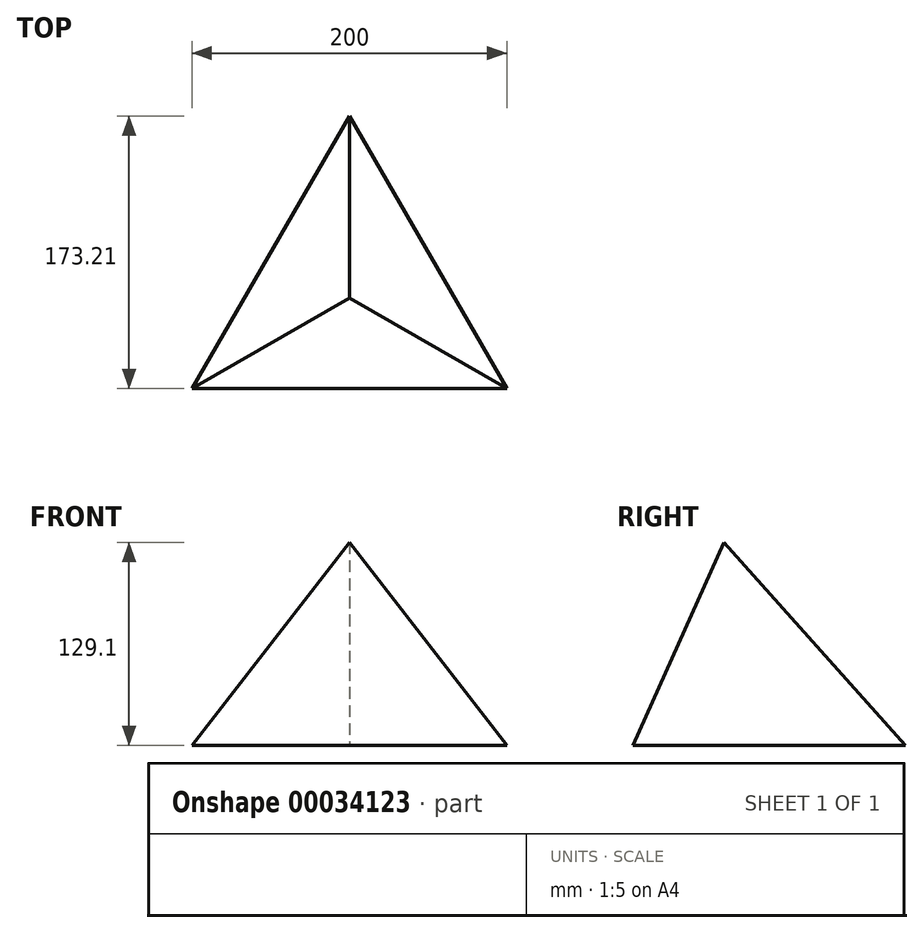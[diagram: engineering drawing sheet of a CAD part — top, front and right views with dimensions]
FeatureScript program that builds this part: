
annotation { "Feature Type Name" : "Feature", "Feature Type Description" : "" }
export const myFeature = defineFeature(function(context is Context, id is Id, definition is map)
    precondition{}
    {
        {
            var Q0;
            Q0=qCreatedBy(makeId("Top.planeOp"),FACE);
            var sketch = newSketch(context, id + "F0", { "sketchPlane" : qUnion([Q0])});
            skLineSegment(sketch, "E0", {"start": v(0, 115.47) * mm, "end": v(100, -57.74) * mm});
            skLineSegment(sketch, "E1", {"start": v(100, -57.74) * mm, "end": v(-100, -57.74) * mm});
            skLineSegment(sketch, "E2", {"start": v(-100, -57.74) * mm, "end": v(0, 115.47) * mm});
            skLineSegment(sketch, "E3", {"start": v(0, 115.47) * mm, "end": v(0, 0) * mm});
            skLineSegment(sketch, "E4", {"start": v(-100, -57.74) * mm, "end": v(0, 0) * mm});
            skLineSegment(sketch, "E5", {"start": v(0, 0) * mm, "end": v(100, -57.74) * mm});
            skPoint(sketch, "E6.orphan", {"position": v(0, -57.74) * mm});
            skSolve(sketch);
        }
        {
            assignVariable(context, id + "F1", {"name" : "Angle", "anyValue" : 65.9});
        }
        {
            var Q0;
            Q0=qSketchRegion(id+"F0",true);
            extrude(context, id + "F2", {"entities" : qUnion([Q0]), "depth" : 1000 * mm, "hasDraft" : true, "draftAngle" : (90 - getVariable(context, 'Angle')) * degree, "draftPullDirection" : true});
        }
    });
